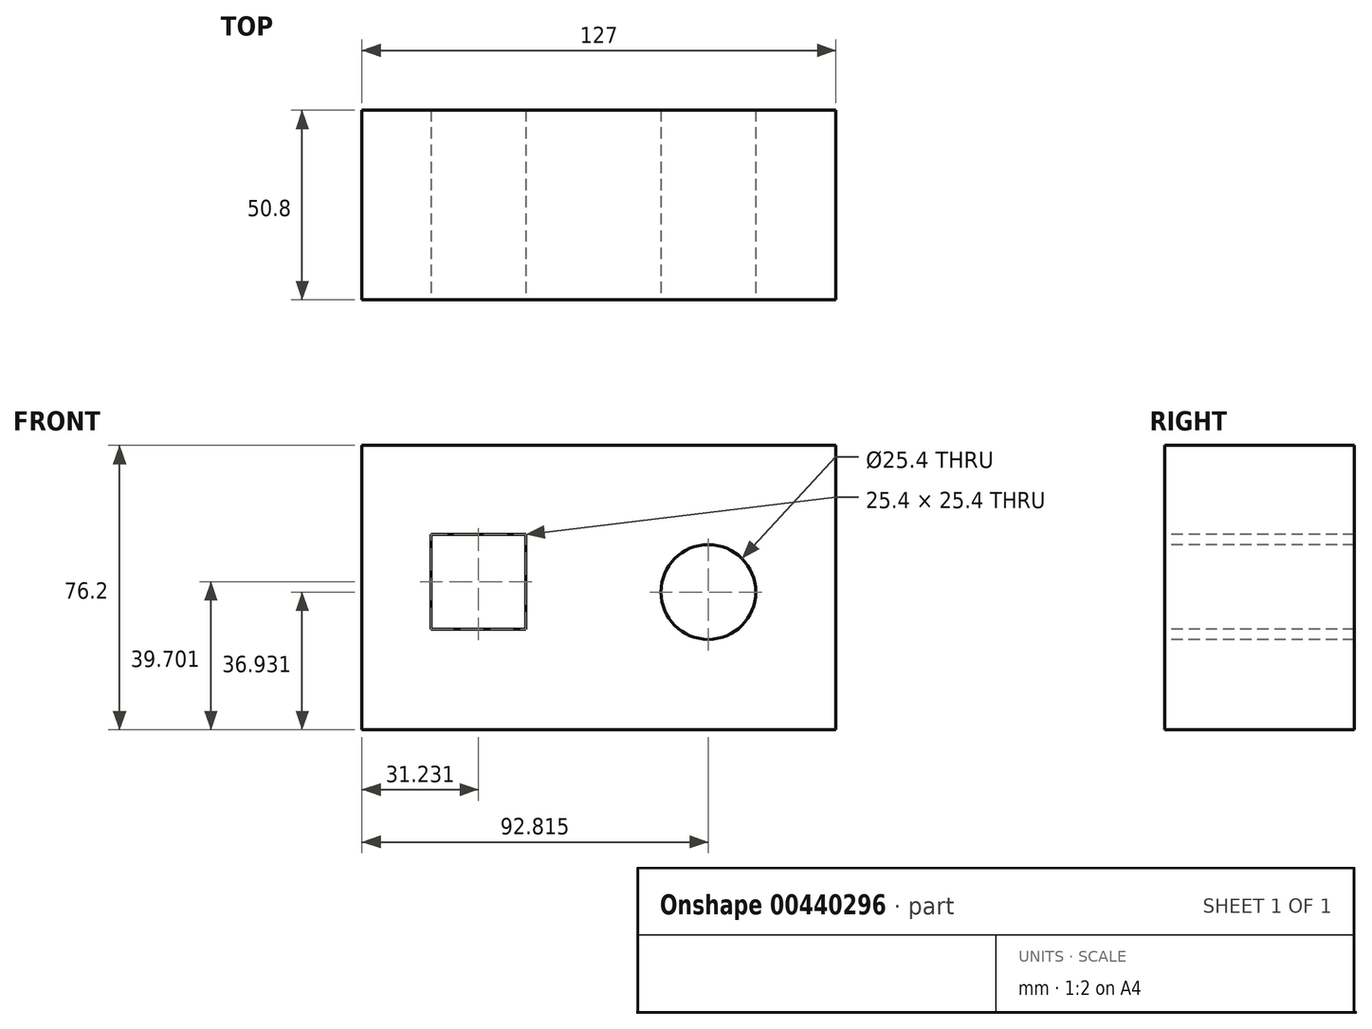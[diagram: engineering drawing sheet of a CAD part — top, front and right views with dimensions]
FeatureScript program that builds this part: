
annotation { "Feature Type Name" : "Feature", "Feature Type Description" : "" }
export const myFeature = defineFeature(function(context is Context, id is Id, definition is map)
    precondition{}
    {
        {
            var Q0;
            Q0=qCreatedBy(makeId("Front.planeOp"),FACE);
            var sketch = newSketch(context, id + "F0", { "sketchPlane" : qUnion([Q0])});
            skLineSegment(sketch, "E0", {"start": v(-67.8, -44.76) * mm, "end": v(59.2, -44.76) * mm});
            skLineSegment(sketch, "E1", {"start": v(-67.8, -44.76) * mm, "end": v(-67.8, 31.44) * mm});
            skLineSegment(sketch, "E2", {"start": v(59.2, -44.76) * mm, "end": v(59.2, 31.44) * mm});
            skLineSegment(sketch, "E3", {"start": v(-67.8, 31.44) * mm, "end": v(59.2, 31.44) * mm});
            skSolve(sketch);
        }
        {
            var Q0;
            Q0 = qSketchRegion(id + "F0", true);
            extrude(context, id + "F1", {"entities" : qUnion([Q0]), "depth" : 50.8 * mm});
        }
        {
            var Q0;
            Q0=makeQuery(id+"F1.opExtrude","CAP_FACE",FACE,{"disambiguationData":[OSD([sQuery(id+"F0.wireOp",EDGE,"E0"),sQuery(id+"F0.wireOp",EDGE,"E1"),sQuery(id+"F0.wireOp",EDGE,"E2"),sQuery(id+"F0.wireOp",EDGE,"E3")])],"isStart":false});
            var sketch = newSketch(context, id + "F2", { "sketchPlane" : qUnion([Q0])});
            skCircle(sketch, "E4", {"center": v(25.02, -7.83) * mm, "radius": 12.7 * mm});
            skLineSegment(sketch, "E5.bottom", {"start": v(-49.27, 7.64) * mm, "end": v(-23.87, 7.64) * mm});
            skLineSegment(sketch, "E5.top", {"start": v(-49.27, -17.76) * mm, "end": v(-23.87, -17.76) * mm});
            skLineSegment(sketch, "E5.left", {"start": v(-49.27, 7.64) * mm, "end": v(-49.27, -17.76) * mm});
            skLineSegment(sketch, "E5.right", {"start": v(-23.87, 7.64) * mm, "end": v(-23.87, -17.76) * mm});
            skSolve(sketch);
        }
        {
            var Q0;
            Q0 = qSketchRegion(id + "F2", true);
            extrude(context, id + "F3", {"entities" : qUnion([Q0]), "operationType" : NewBodyOperationType.REMOVE, "oppositeDirection" : true, "depth" : 50.8 * mm});
        }
    });
